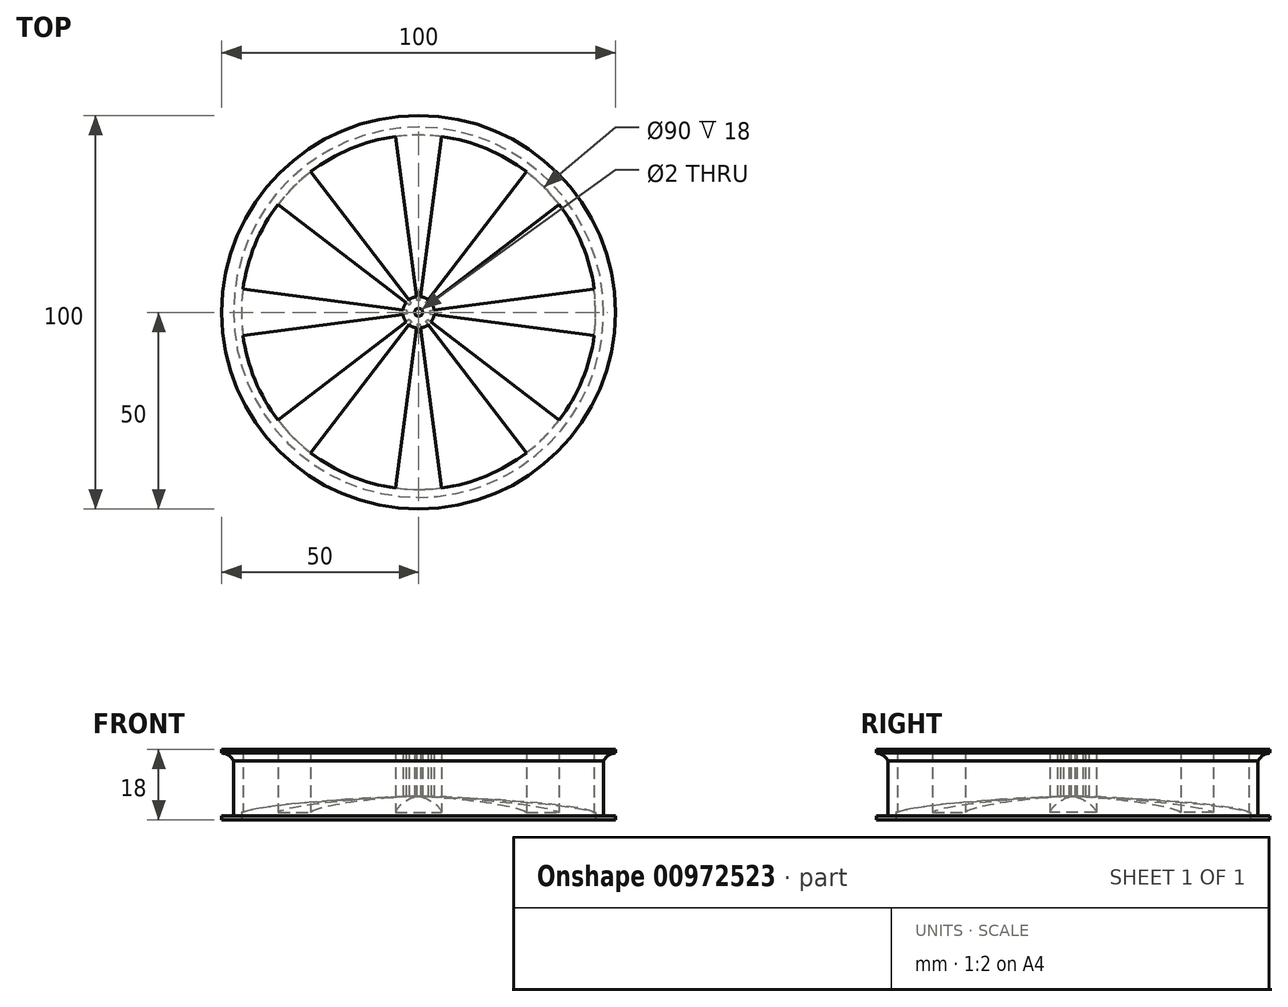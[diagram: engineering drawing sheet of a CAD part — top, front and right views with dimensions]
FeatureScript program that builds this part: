
annotation { "Feature Type Name" : "Feature", "Feature Type Description" : "" }
export const myFeature = defineFeature(function(context is Context, id is Id, definition is map)
    precondition{}
    {
        {
            var Q0;
            Q0=qCreatedBy(makeId("Top.planeOp"),FACE);
            var sketch = newSketch(context, id + "F0", { "sketchPlane" : qUnion([Q0])});
            skCircle(sketch, "E0", {"center": v(0, 0) * mm, "radius": 47 * mm});
            skCircle(sketch, "E1", {"center": v(0, 0) * mm, "radius": 50 * mm});
            skCircle(sketch, "E2", {"center": v(0, 0) * mm, "radius": 1 * mm});
            skCircle(sketch, "E3", {"center": v(0, 0) * mm, "radius": 45 * mm});
            skCircle(sketch, "E4", {"center": v(0, 0) * mm, "radius": 4 * mm});
            skArc(sketch, "E5", {"start": v(7.17, -0.88) * mm, "mid": v(7.22, 0) * mm, "end": v(7.17, 0.88) * mm});
            skLineSegment(sketch, "E6", {"start": v(0, 0) * mm, "end": v(26.75, -3.28) * mm, "construction": true});
            skLineSegment(sketch, "E7", {"start": v(-21, 0) * mm, "end": v(30.4, 0) * mm, "construction": true});
            skLineSegment(sketch, "E8.MirrorCS", {"start": v(0, 0) * mm, "end": v(26.75, 3.28) * mm, "construction": true});
            skSolve(sketch);
        }
        {
            var Q0;
            Q0=makeQuery(id+"F0.imprint","IMPRINT",FACE,{"disambiguationData":[TD([[makeQuery(id+"F0.imprint","IMPRINT",EDGE,{"derivedFrom":sQuery(id+"F0.wireOp",EDGE,"E0")}),1.0]])]});
            extrude(context, id + "F1", {"entities" : qUnion([Q0]), "endBound" : BoundingType.SYMMETRIC, "depth" : 18 * mm, "offsetDistance" : 25 * mm});
        }
        {
            var Q0;
            Q0=makeQuery(id+"F0.imprint","IMPRINT",FACE,{"disambiguationData":[TD([[makeQuery(id+"F0.imprint","IMPRINT",EDGE,{"derivedFrom":sQuery(id+"F0.wireOp",EDGE,"E2")}),-1.0]])]});
            extrude(context, id + "F2", {"entities" : qUnion([Q0]), "depth" : 9 * mm, "offsetDistance" : 25 * mm, "hasSecondDirection" : true, "secondDirectionOppositeDirection" : true, "secondDirectionDepth" : 3 * mm});
        }
        {
            var Q0;
            Q0=makeQuery(id+"F0.imprint","IMPRINT",FACE,{"disambiguationData":[TD([[makeQuery(id+"F0.imprint","IMPRINT",EDGE,{"derivedFrom":sQuery(id+"F0.wireOp",EDGE,"E0")}),-1.0]])]});
            extrude(context, id + "F3", {"entities" : qUnion([Q0]), "operationType" : NewBodyOperationType.ADD, "depth" : 9 * mm, "offsetDistance" : 25 * mm, "hasSecondDirection" : true, "secondDirectionOppositeDirection" : false, "secondDirectionDepth" : 8 * mm});
        }
        {
            var Q0;
            Q0=makeQuery(id+"F0.imprint","IMPRINT",FACE,{"disambiguationData":[TD([[makeQuery(id+"F0.imprint","IMPRINT",EDGE,{"derivedFrom":sQuery(id+"F0.wireOp",EDGE,"E0")}),-1.0]])]});
            extrude(context, id + "F4", {"entities" : qUnion([Q0]), "operationType" : NewBodyOperationType.ADD, "oppositeDirection" : true, "depth" : 9 * mm, "offsetDistance" : 25 * mm, "hasSecondDirection" : true, "secondDirectionOppositeDirection" : true, "secondDirectionDepth" : 8 * mm});
        }
        {
            var Q0;
            Q0=qCreatedBy(makeId("Front.planeOp"),FACE);
            var sketch = newSketch(context, id + "F5", { "sketchPlane" : qUnion([Q0])});
            skLineSegment(sketch, "E9", {"start": v(3, 32.78) * mm, "end": v(3, -36.48) * mm, "construction": true});
            skLineSegment(sketch, "E10", {"start": v(-37.51, -3) * mm, "end": v(51.54, -3) * mm, "construction": true});
            skLineSegment(sketch, "E11", {"start": v(46, 33.34) * mm, "end": v(46, -34.72) * mm, "construction": true});
            skLineSegment(sketch, "E12", {"start": v(-42.78, 9) * mm, "end": v(59.03, 9) * mm, "construction": true});
            skPoint(sketch, "E13.1.internal.snap0", {"position": v(3, -1.85) * mm});
            skFitSpline(sketch, "E13", {"points": [v(0, -3) * mm, v(3, -3) * mm, v(46, -7.98) * mm, v(6.63, -19.5) * mm], "startDerivative": vector(11.2, 1.75) * mm, "endDerivative": vector(-27.98, -30.57) * mm});
            skLineSegment(sketch, "E14", {"start": v(3, 9) * mm, "end": v(3, -3) * mm});
            skLineSegment(sketch, "E15", {"start": v(46, -7.82) * mm, "end": v(46, 9) * mm});
            skLineSegment(sketch, "E16", {"start": v(0, 18.34) * mm, "end": v(0, -23.8) * mm, "construction": true});
            skLineSegment(sketch, "E17", {"start": v(59.38, 6) * mm, "end": v(13.4, 6) * mm, "construction": true});
            skLineSegment(sketch, "E18", {"start": v(50, 15.46) * mm, "end": v(50, -6.78) * mm, "construction": true});
            skArc(sketch, "E19", {"start": v(50, 8) * mm, "mid": v(48.22, 7.42) * mm, "end": v(47, 6) * mm});
            skLineSegment(sketch, "E20", {"start": v(47, 6) * mm, "end": v(47, 8) * mm});
            skLineSegment(sketch, "E21", {"start": v(47, 8) * mm, "end": v(50, 8) * mm});
            skArc(sketch, "E22.MirrorCS", {"start": v(50, -8) * mm, "mid": v(48.22, -7.42) * mm, "end": v(47, -6) * mm});
            skLineSegment(sketch, "E23.MirrorCS", {"start": v(47, -2.29) * mm, "end": v(47, -17.57) * mm, "construction": true});
            skLineSegment(sketch, "E24.MirrorCS", {"start": v(26.03, -8) * mm, "end": v(7.62, -8) * mm, "construction": true});
            skLineSegment(sketch, "E25.MirrorCS", {"start": v(47, -6) * mm, "end": v(47, -8) * mm});
            skLineSegment(sketch, "E26.MirrorCS", {"start": v(47, -8) * mm, "end": v(50, -8) * mm});
            skLineSegment(sketch, "E27", {"start": v(3, 9) * mm, "end": v(46, 9) * mm});
            skSolve(sketch);
        }
        {
            var Q0;
            {var subQ2=sQuery(id+"F5.wireOp",EDGE,"E14");Q0=makeQuery(id+"F5.imprint","IMPRINT",FACE,{"disambiguationData":[TD([[makeQuery(id+"F5.imprint","IMPRINT",EDGE,{"derivedFrom":subQ2}),1.0]])]});}
            var Q1;
            Q1=sQuery(id+"F5.wireOp",EDGE,"E16");
            revolve(context, id + "F6", {"surfaceOperationType" : NewSurfaceOperationType.NEW, "entities" : qUnion([Q0]), "axis" : qUnion([Q1]), "revolveType" : RevolveType.SYMMETRIC, "angle" : 15 * degree});
        }
        {
            var Q0;
            Q0=makeQuery(id+"F6.opRevolve","SWEPT_BODY",BODY,{"disambiguationData":[OSD([sQuery(id+"F5.wireOp",EDGE,"E13"),sQuery(id+"F5.wireOp",EDGE,"CZLmqUYp-TeBy-6FCv-n9f3-z11s9wL4hSry"),sQuery(id+"F5.wireOp",EDGE,"E14"),sQuery(id+"F5.wireOp",EDGE,"E15")])]});
            var Q1;
            Q1=sQuery(id+"F5.wireOp",EDGE,"E16");
            circularPattern(context, id + "F7", {"operationType" : NewBodyOperationType.ADD, "entities" : qUnion([Q0]), "axis" : qUnion([Q1]), "angle" : 360 * degree, "instanceCount" : 8, "equalSpace" : true});
        }
        {
            var Q0;
            Q0=makeQuery(id+"F5.imprint","IMPRINT",FACE,{"disambiguationData":[TD([[makeQuery(id+"F5.imprint","IMPRINT",EDGE,{"derivedFrom":sQuery(id+"F5.wireOp",EDGE,"E19")}),-1.0]])]});
            var Q1;
            Q1=makeQuery(id+"F5.imprint","IMPRINT",FACE,{"disambiguationData":[TD([[makeQuery(id+"F5.imprint","IMPRINT",EDGE,{"derivedFrom":sQuery(id+"F5.wireOp",EDGE,"E22.MirrorCS")}),1.0]])]});
            var Q2;
            Q2=sQuery(id+"F5.wireOp",EDGE,"E16");
            revolve(context, id + "F8", {"operationType" : NewBodyOperationType.ADD, "surfaceOperationType" : NewSurfaceOperationType.NEW, "entities" : qUnion([Q0, Q1]), "axis" : qUnion([Q2]), "revolveType" : RevolveType.FULL});
        }
    });
